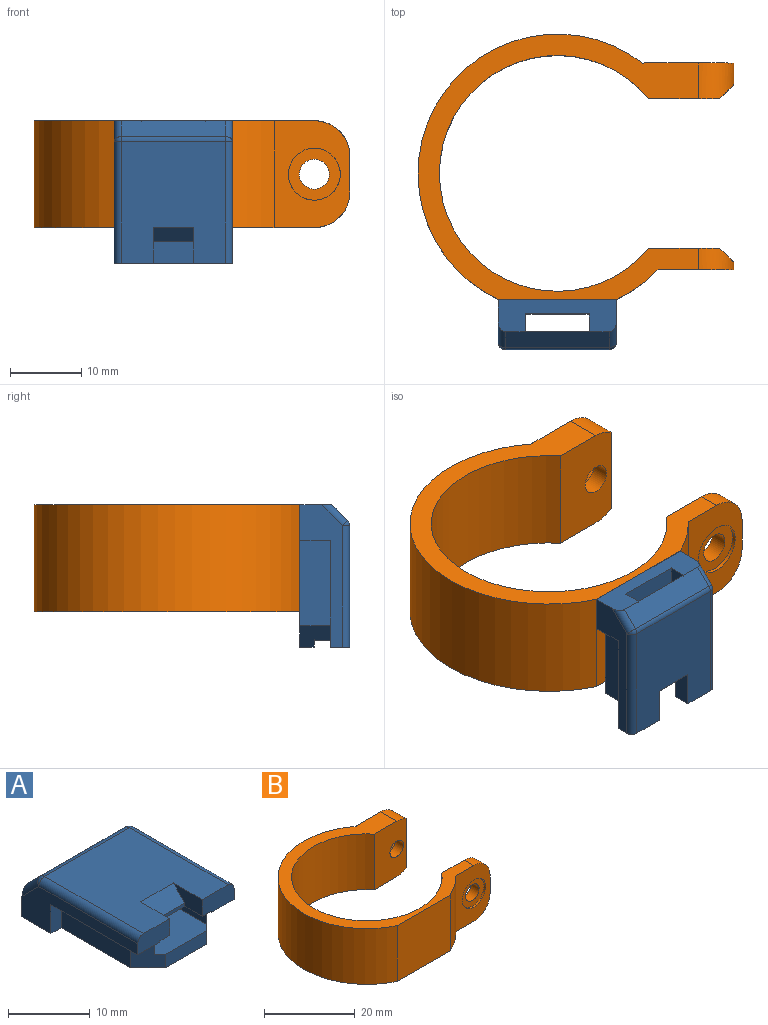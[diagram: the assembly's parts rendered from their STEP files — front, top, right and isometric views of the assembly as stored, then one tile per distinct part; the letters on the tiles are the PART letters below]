
ASSEMBLY  parts=2 mates=1
PART A: 32 faces, bbox 16.6x20.7x7 mm
  f0: plane 7.1x2mm, normal (0,-1,0), area 14.2mm2, adj f8,f24,f30,f31
  f1: plane 5.47x2.7mm, normal (0,-1,0), area 14.2mm2, adj f3,f7,f10,f15,f23,f25,f27
  f2: plane 5.47x2.7mm, normal (0,-1,0), area 14.2mm2, adj f3,f6,f13,f18,f22,f25,f26
  f3: plane 17.09x14.6mm, normal (0,0,1), area 221.2mm2, adj f1,f2,f15,f18,f19,f26,f27,f29
  f4: plane 16.6x4.5mm, normal (0,1,0), area 51.6mm2, adj f6,f7,f8,f14,f16,f21,f22,f23
  f5: plane 4.3x1.75mm, normal (0,-1,0), area 7.5mm2, adj f6,f8,f12,f13
  f6: plane 20x6mm, normal (1,0,0), area 51.3mm2, adj f2,f4,f5,f8,f13,f18,f21
  f7: plane 20x6mm, normal (-1,0,0), area 51.3mm2, adj f1,f4,f8,f9,f10,f15,f16
  f8: plane 20x16.6mm, normal (0,0,-1), area 270.5mm2, adj f0,f4,f5,f6,f7,f9,f11,f12
  f9: plane 4.3x1.75mm, normal (0,-1,0), area 7.5mm2, adj f7,f8,f10,f11
  f10: plane 15x3.8mm, normal (0,0,-1), area 30.3mm2, adj f1,f7,f9,f11,f23,f30
  f11: plane 12x4.3mm, normal (-1,0,0), area 51.6mm2, adj f8,f9,f10,f30
  f12: plane 12x4.3mm, normal (1,0,0), area 51.6mm2, adj f5,f8,f13,f31
  f13: plane 15x3.8mm, normal (0,0,-1), area 30.3mm2, adj f2,f5,f6,f12,f22,f31
  f14: plane 14.6x2.21mm, normal (0,0.71,0.71), area 45.6mm2, adj f4,f16,f19,f21,f25
  f15: cylinder r=1mm len=17.09mm, axis (0,-1,0), area 26.8mm2, adj f1,f3,f7,f17
  f16: cylinder r=1mm len=3.62mm, axis (0,0.71,-0.71), area 5.5mm2, adj f4,f7,f14,f17
  f17: sphere r=1mm, area 0.8mm2, adj f15,f16,f19
  f18: cylinder r=1mm len=17.09mm, axis (0,1,0), area 26.8mm2, adj f2,f3,f6,f20
  f19: cylinder r=1mm len=14.6mm, axis (-1,0,0), area 11.5mm2, adj f3,f14,f17,f20
  f20: sphere r=1mm, area 0.8mm2, adj f18,f19,f21
  f21: cylinder r=1mm len=3.62mm, axis (0,0.71,-0.71), area 5.5mm2, adj f4,f6,f14,f20
  f22: plane 20x2.5mm, normal (-1,0,0), area 47.8mm2, adj f2,f4,f13,f24,f25,f31
  f23: plane 20x2.5mm, normal (1,0,0), area 47.8mm2, adj f1,f4,f10,f24,f25,f30
  f24: plane 20x9mm, normal (0,0,1), area 179.1mm2, adj f0,f4,f22,f23,f30,f31
  f25: plane 20x9mm, normal (0,0,-1), area 163mm2, adj f1,f2,f14,f22,f23,f26,f27,f28
  f26: plane 5x2.5mm, normal (-1,0,0), area 9.5mm2, adj f2,f3,f25,f28,f29
  f27: plane 5x2.5mm, normal (1,0,0), area 9.5mm2, adj f1,f3,f25,f28,f29
  f28: plane 5.66x0.5mm, normal (0,-1,0), area 2.8mm2, adj f25,f26,f27,f29
  f29: plane 5.66x2mm, normal (0,-0.71,0.71), area 16mm2, adj f3,f26,f27,f28
  f30: plane 4.3x3mm, normal (-0.71,-0.71,0), area 15.2mm2, adj f0,f8,f10,f11,f23,f24
  f31: plane 4.3x3mm, normal (0.71,-0.71,0), area 15.2mm2, adj f0,f8,f12,f13,f22,f24
PART B: 30 faces, bbox 44.3x37.3x15 mm
  f0: cylinder r=19.55mm len=37.27mm, axis (0,0,-1), area 988.3mm2, adj f4,f5,f24,f29
  f1: cylinder r=2.1mm len=4.2mm, axis (0,-1,0), area 33mm2, adj f7,f13
  f2: cylinder r=19.55mm len=15mm, axis (0,0,-1), area 109.4mm2, adj f4,f5,f10,f24
  f3: cylinder r=16.55mm len=33.1mm, axis (0,0,-1), area 1218.6mm2, adj f4,f5,f6,f7
  f4: plane 39.34x37.27mm, normal (0,0,1), area 292.5mm2, adj f0,f2,f3,f6,f7,f9,f10,f24
  f5: plane 39.34x37.27mm, normal (0,0,-1), area 292.5mm2, adj f0,f2,f3,f6,f7,f9,f10,f24
  f6: plane 15x10mm, normal (0,1,0), area 134.2mm2, adj f3,f4,f5,f12,f22,f26,f27
  f7: plane 15x10mm, normal (0,-1,0), area 134.2mm2, adj f1,f3,f4,f5,f23,f25,f28
  f8: plane 5x3mm, normal (1,0,0), area 15mm2, adj f9,f23,f25,f28
  f9: plane 15x12.52mm, normal (0,1,0), area 133.4mm2, adj f4,f5,f8,f14,f15,f16,f17,f18
  f10: plane 15x10.65mm, normal (0,-1,0), area 107.2mm2, adj f2,f4,f5,f11,f21,f26,f27
  f11: plane 5x1mm, normal (1,0,0), area 5mm2, adj f10,f22,f26,f27
  f12: cylinder r=2.1mm len=4.2mm, axis (0,-1,0), area 33mm2, adj f6,f20
  f13: plane 8.2x7.1mm, normal (0,1,0), area 29.8mm2, adj f1,f14,f15,f16,f17,f18,f19
  f14: plane 4.1x2.5mm, normal (1,0,0), area 10.2mm2, adj f9,f13,f15,f19
  f15: plane 3.55x2.5mm, normal (0.5,0,-0.87), area 10.2mm2, adj f9,f13,f14,f16
  f16: plane 3.55x2.5mm, normal (-0.5,0,-0.87), area 10.2mm2, adj f9,f13,f15,f17
  f17: plane 4.1x2.5mm, normal (-1,0,0), area 10.2mm2, adj f9,f13,f16,f18
  f18: plane 3.55x2.5mm, normal (-0.5,0,0.87), area 10.2mm2, adj f9,f13,f17,f19
  f19: plane 3.55x2.5mm, normal (0.5,0,0.87), area 10.2mm2, adj f9,f13,f14,f18
  f20: plane 7.3x7.3mm, normal (0,-1,0), area 28mm2, adj f12,f21
  f21: cylinder r=3.65mm len=7.3mm, axis (0,-1,0), area 11.5mm2, adj f10,f20
  f22: plane 13x2mm, normal (0.71,0.71,0), area 30mm2, adj f6,f11,f26,f27
  f23: plane 13x2mm, normal (0.71,-0.71,0), area 30mm2, adj f7,f8,f25,f28
  f24: plane 16.5x15mm, normal (0,-1,0), area 247.5mm2, adj f0,f2,f4,f5
  f25: cylinder r=5mm len=5mm, axis (0,1,0), area 33.2mm2, adj f4,f7,f8,f9,f23
  f26: cylinder r=5mm len=5mm, axis (0,1,0), area 17.5mm2, adj f4,f6,f10,f11,f22
  f27: cylinder r=5mm len=5mm, axis (0,1,0), area 17.5mm2, adj f5,f6,f10,f11,f22
  f28: cylinder r=5mm len=5mm, axis (0,1,0), area 33.2mm2, adj f5,f7,f8,f9,f23
  f29: plane 15x0.22mm, normal (-0.44,0.9,0), area 3.7mm2, adj f0,f4,f5,f9
PLACE A rot(axis=(1,0,0),90deg) t=(0,-21.22,5)mm
PLACE B at identity fixed
MATE fastened B.f24 <-> A.f8  axis (0,-1,0) through (0,-17.72,10)mm
